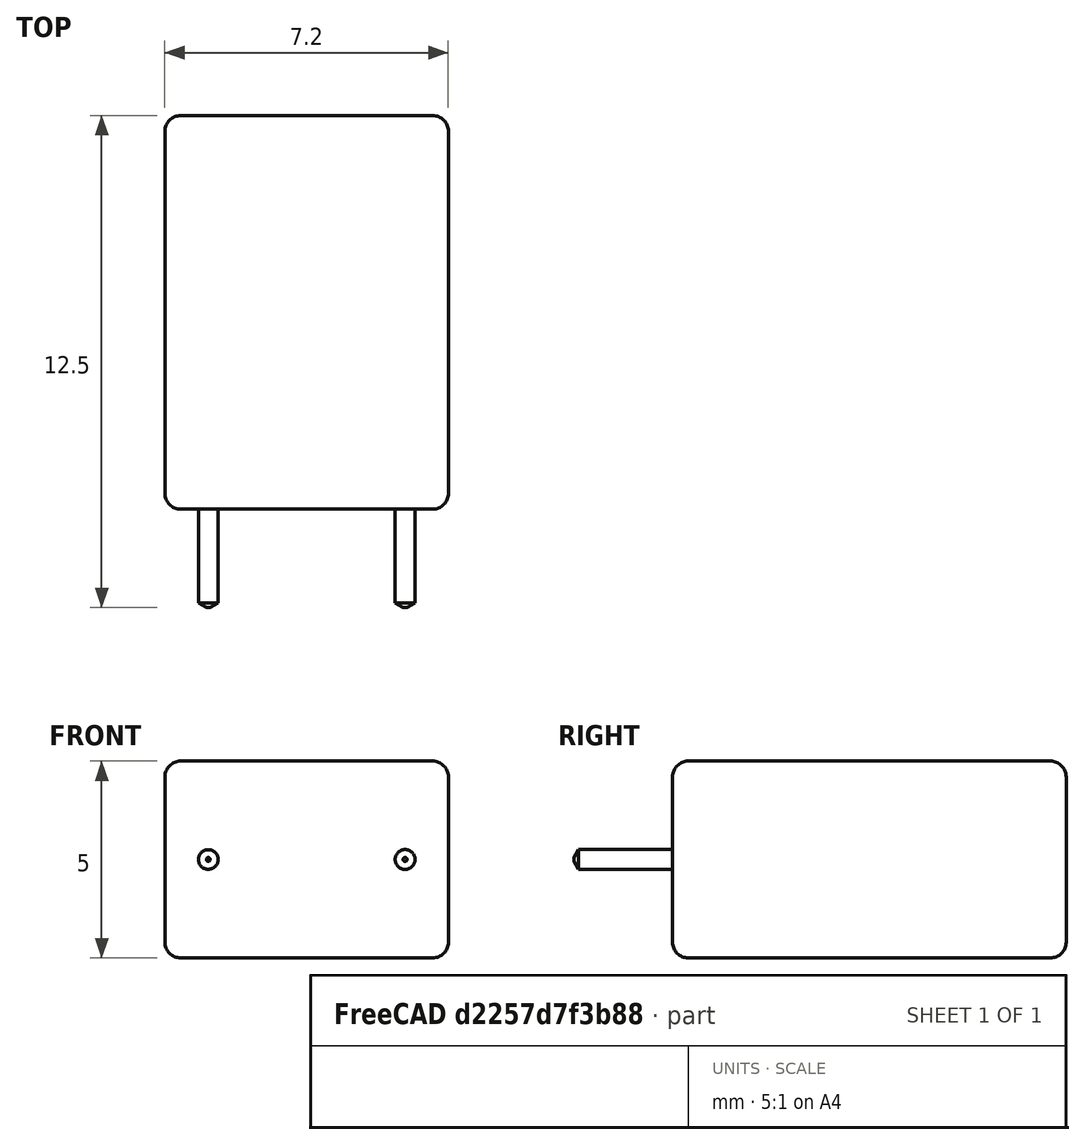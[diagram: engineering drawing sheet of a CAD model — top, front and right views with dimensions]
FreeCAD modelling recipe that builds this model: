
FCSTD DOCUMENT  (FreeCAD 0.17R13528 (Git))
Label: WIMA_F_Case
License: All rights reserved
LicenseURL: http://en.wikipedia.org/wiki/All_rights_reserved
objects: Part::Part2DObjectPython×6, Part::Feature×1
note: 7 computed .brp shape members not serialized (recipe doc carries the construction recipe); baked Part::Feature solids carry a one-line shape summary decoded from their .brp

FEATURE [Part::Part2DObjectPython] ShapeString  label="F_WIMA"  # Draft 2D object (typed FeaturePython)
  FontFile = <userpath>/Desktop/Freecad Projects/calibrib.ttf
  Placement = pos=(-0.75,3.5,2.51) rot=(0,0,1;0rad)
  Size = 1.75
  String = WIMA
  Tracking = 0
FEATURE [Part::Part2DObjectPython] ShapeString001  label="F_Vaule/Rating"  # Draft 2D object (typed FeaturePython)
  FontFile = <userpath>/Desktop/Freecad Projects/calibrib.ttf
  Placement = pos=(-0.65,2.25,2.51) rot=(0,0,1;0rad)
  Size = 1
  String = 1.0µ/63V
  Tracking = 0
FEATURE [Part::Part2DObjectPython] ShapeString002  label="F_Tolerance"  # Draft 2D object (typed FeaturePython)
  FontFile = <userpath>/Desktop/Freecad Projects/calibrib.ttf
  Placement = pos=(-0.65,1,2.51) rot=(0,0,1;0rad)
  Size = 1
  String = 10
  Tracking = 0
FEATURE [Part::Part2DObjectPython] ShapeString003  label="B_WIMA"  # Draft 2D object (typed FeaturePython)
  FontFile = <userpath>/Desktop/Freecad Projects/calibrib.ttf
  Placement = pos=(5,3.5,-2.51) rot=(0,1,0;3.14159rad)
  Size = 1.75
  String = WIMA
  Tracking = 0
FEATURE [Part::Part2DObjectPython] ShapeString004  label="B_Value/Tolerance"  # Draft 2D object (typed FeaturePython)
  FontFile = <userpath>/Desktop/Freecad Projects/calibrib.ttf
  Placement = pos=(4.9,2.25,-2.51) rot=(0,1,0;3.14159rad)
  Size = 1
  String = 1.0µ/63V
  Tracking = 0
FEATURE [Part::Part2DObjectPython] ShapeString005  label="B_Tolerance"  # Draft 2D object (typed FeaturePython)
  FontFile = <userpath>/Desktop/Freecad Projects/calibrib.ttf
  Placement = pos=(4.9,1,-2.51) rot=(0,1,0;3.14159rad)
  Size = 1
  String = 10
  Tracking = 0
FEATURE [Part::Feature] Part__Feature  label="WIMA_F_Case"
  shape: bbox 7.2 x 12.5 x 5 mm, 36 faces (baked)
